# Revit family: Ворота ВПР-60
name_source: partatom
category: Двери
revit_build: Autodesk Revit 2017 (Build: 20160225_1515(x64)
units: mm (PartAtom-declared; Revit-internal decimal feet)

## family parameters
Всегда вертикально = Да
Заголовок OmniClass = Doors
Номер OmniClass = 23.30.10.00
Общий = Нет
Основа = Стена
При загрузке вырезать с полостями = Нет
Точка расчета площади = Нет

## types (12) — shared parameters
ADSK_Завод-изготовитель = ДВР Центр, г.Москва
ADSK_Наименование = ВПР-ОГНЕДЕКОР-60К
ADSK_Наименование краткое = ВПР-60
ADSK_Обозначение = ГОСТ 31174-2003, ГОСТ 53307-2009
ADSK_Предел огнестойкости = EI-60
URL = http://dwrcenter.ru
Высокий порог = 50 мм
Высота порога = 30 мм
Группа модели = Ворота
Замыкание стены = По основе
Заполнение монтажного зазора = <По категории>
Изготовитель = ДВР Центр, г.Москва, +7-495-4-112-911
Материал коробки = <По категории>
Материал наличника = Отделка. Орех
Материал створки = <По категории>
Монтажный зазор сверху = 25 мм
Монтажный зазор слева = 25 мм
Монтажный зазор справа = 25 мм
Наличник с внутренней стороны = Да
Наличник с наружной стороны = Да
Огнестойкость = EI-60
Описание = Ворота противопожарные распашные
Порог с притвором = Да
Телефоны изготовителя = +7-495-4-112-911, +7-495-5-103-206
Тип конструкций = Ворота противопожарные распашные, ГОСТ 53307-2009
Толщина = 135 мм
Функция = Внутренние слои
Ширина наличника = 60 мм
zero-valued in all types: ADSK_Количество, ADSK_Откосы_Глубина, ADSK_Толщина стены, ADSK_Толщина стены (отчет)

## per-type parameters (varying)
| type | ADSK_URL страницы изделия | ADSK_Открывание | Высота | Высота ворот | Высота полосы | Левая | Правая | Ширина | Ширина С1 | Ширина С2 | Ширина ворот | Ширина ответной створки | Ширина правой створки | Ширина створок в равнопольной двери |
| ВПР-ОГНЕДЕКОР-90, ПТ, проем 2500х2500 | http://www.dwrcenter.ru | Правая | 2500 мм | 2475 мм | 825 мм | Нет | Да | 2500 мм | 1170 мм | 1170 мм | 2450 мм | 1170 мм | 1170 мм | 1170 мм |
| ВПР-ОГНЕДЕКОР-90, ЛТ, проем 2500х2500 | http://www.dwrcenter.ru | Левая | 2500 мм | 2475 мм | 825 мм | Да | Нет | 2500 мм | 1170 мм | 1170 мм | 2450 мм | 1170 мм | 1170 мм | 1170 мм |
| ВПР-ОГНЕДЕКОР-90, ПТ, проем 2500х3000 | http://www.dwrcenter.ru | Правая | 3000 мм | 2975 мм | 992 мм | Нет | Да | 2500 мм | 1170 мм | 1170 мм | 2450 мм | 1170 мм | 1170 мм | 1170 мм |
| ВПР-ОГНЕДЕКОР-90, ЛТ, проем 2500х3000 | http://www.dwrcenter.ru | Левая | 3000 мм | 2975 мм | 992 мм | Да | Нет | 2500 мм | 1170 мм | 1170 мм | 2450 мм | 1170 мм | 1170 мм | 1170 мм |
| ВПР-ОГНЕДЕКОР-90, ПТ, проем 3000х3000 | http://www.dwrcenter.ru | Правая | 3000 мм | 2975 мм | 992 мм | Нет | Да | 3000 мм | 1420 мм | 1420 мм | 2950 мм | 1420 мм | 1420 мм | 1420 мм |
| ВПР-ОГНЕДЕКОР-90, ЛТ, проем 3000х3000 | http://www.dwrcenter.ru | Левая | 3000 мм | 2975 мм | 992 мм | Да | Нет | 3000 мм | 1420 мм | 1420 мм | 2950 мм | 1420 мм | 1420 мм | 1420 мм |
| ВПР-ОГНЕДЕКОР-90, ПТ, проем 3000х3500 | http://dwrcenter.ru | Правая | 3500 мм | 3475 мм | 1158 мм | Нет | Да | 3000 мм | 1420 мм | 1420 мм | 2950 мм | 1420 мм | 1420 мм | 1420 мм |
| ВПР-ОГНЕДЕКОР-90, ЛТ, проем 3000х3500 | http://www.dwrcenter.ru | Левая | 3500 мм | 3475 мм | 1158 мм | Да | Нет | 3000 мм | 1420 мм | 1420 мм | 2950 мм | 1420 мм | 1420 мм | 1420 мм |
| ВПР-ОГНЕДЕКОР-90, ПТ, проем 3500х3500 | http://www.dwrcenter.ru | Правая | 3500 мм | 3475 мм | 1158 мм | Нет | Да | 3500 мм | 1670 мм | 1670 мм | 3450 мм | 1670 мм | 1670 мм | 1670 мм |
| ВПР-ОГНЕДЕКОР-90, ЛТ, проем 3500х3500 | http://www.dwrcenter.ru | Левая | 3500 мм | 3475 мм | 1158 мм | Да | Нет | 3500 мм | 1670 мм | 1670 мм | 3450 мм | 1670 мм | 1670 мм | 1670 мм |
| ВПР-ОГНЕДЕКОР-90, ПТ, проем 3500х4000 | http://www.dwrcenter.ru | Правая | 4000 мм | 3975 мм | 1325 мм | Нет | Да | 3500 мм | 1670 мм | 1670 мм | 3450 мм | 1670 мм | 1670 мм | 1670 мм |
| ВПР-ОГНЕДЕКОР-90, ЛТ, проем 3500х4000 | http://www.dwrcenter.ru | Левая | 4000 мм | 3975 мм | 1325 мм | Да | Нет | 3500 мм | 1670 мм | 1670 мм | 3450 мм | 1670 мм | 1670 мм | 1670 мм |
